# Revit family: BuroSeating_Harmony 5 Star
name_source: partatom
category: Furniture
units: mm (PartAtom-declared; Revit-internal decimal feet)

## family parameters
Always vertical = Yes
Cut with Voids When Loaded = No
OmniClass Number = 23.40.70.14.64.11
OmniClass Title = Office Furniture
Room Calculation Point = No
Shared = Yes
Work Plane-Based = No

## types (2) — shared parameters
Assembly Code = E2020
BackSupportMaterial = BuroSeating_Plastic_Light Grey
CastorWheelMaterial = BuroSeating_Plastic_Dark Grey
FrameMaterial = BuroSeating_Aluminium_Black
Manufacturer = Buro Seating
NominalDepth = 595 mm
NominalHeight = 850 mm
NominalSeatHeight = 415-535h
NominalWidth = 625 mm  [stored 2.05052 ft]
ProductGroup = 5 Star
ProductPageURL AU = https://buroseating.com
ProductPageURL NZ = https://buroseating.co.nz
ProductRange = Harmony
SeatDepth = 470 mm  [stored 1.54199 ft]
SeatLeverFrameMaterial = BuroSeating_Aluminium_Black
SeatLeverHandleMaterial = BuroSeating_Aluminium_Black
SeatWidth = 470 mm  [stored 1.54199 ft]
TopLiftMaterial = BuroSeating_Metal_Chrome_Semi-Polished
Type Comments = Seat Height 430-520mm High
URL = https://buroseating.co.nz
URL AU = https://buroseating.com
WarrantyDescription = Full 5 year guarantee (excluding upholstery)
zero-valued in all types: Default Elevation

## per-type parameters (varying)
| type | ArmRestMaterial | ArmRestSupportMaterial | BackFrameMaterial | BackPanelMaterial | BackRestMaterial | BaseMaterial | BottomLiftMaterial | CastorMaterial | Description | Model | SeatMaterial | SeatSupportMaterial | SeatTiltMaterial |
| Harmony 5 Star KON173-2-12 | BuroSeating_Plastic_Black | BuroSeating_Plastic_Black | BuroSeating_Plastic_Black | BuroSeating_Fabric_Mesh_Black | BuroSeating_Fabric_Mesh_Black | BuroSeating_Aluminium_Black | BuroSeating_Plastic_Black | BuroSeating_Plastic_Black | Harmony 5 Star Black/Black P/C | KON173-2-12 | BuroSeating_Fabric_Black | BuroSeating_Plastic_Black | BuroSeating_Aluminium_Black |
| Harmony 5 Star KON173-3-13 | BuroSeating_Plastic_Grey | BuroSeating_Plastic_Light Grey | BuroSeating_Plastic_Light Grey | BuroSeating_Fabric_Mesh_Grey | BuroSeating_Fabric_Mesh_Grey | BuroSeating_Metal_Chrome_Semi-Polished | BuroSeating_Plastic_Light Grey | BuroSeating_Plastic_Light Grey | Harmony 5 Star Light Grey / Ali Base | Harmony 5 Star KON173-3-13 | BuroSeating_Fabric_BlueGrey | BuroSeating_Plastic_Light Grey | BuroSeating_Plastic_Light Grey |

note: [stored X ft] marks values corroborated as IEEE doubles in the binary element streams (Revit-internal decimal feet)

## geometry (parser evidence)
native form markers: Sweep x6
no freeform markers — native parametric forms only
